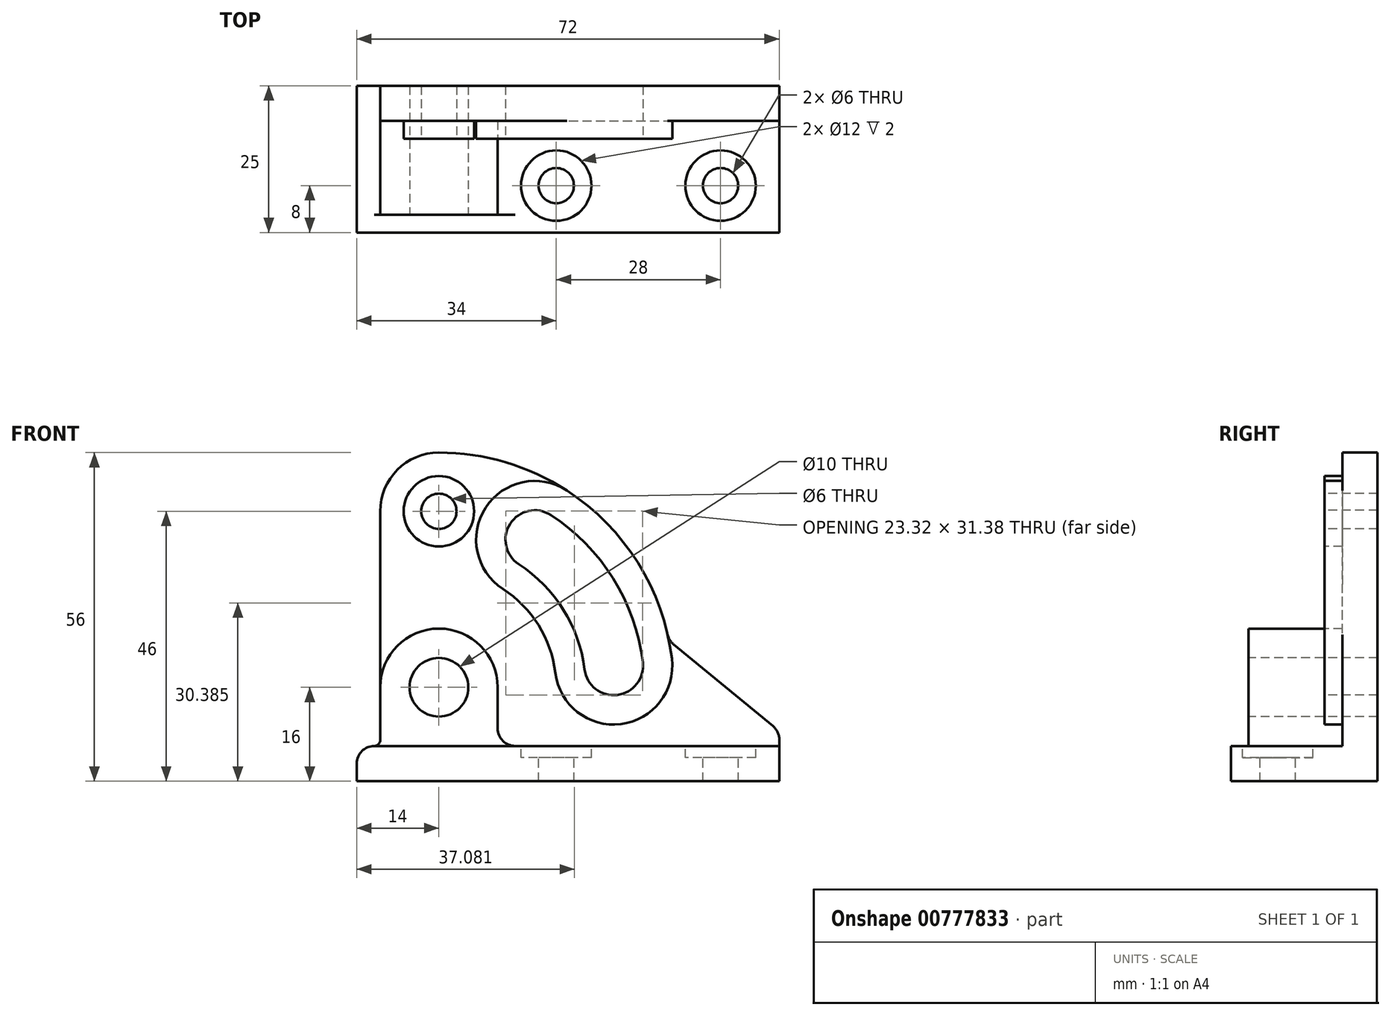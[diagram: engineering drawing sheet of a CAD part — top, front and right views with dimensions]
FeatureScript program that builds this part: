
annotation { "Feature Type Name" : "Feature", "Feature Type Description" : "" }
export const myFeature = defineFeature(function(context is Context, id is Id, definition is map)
    precondition{}
    {
        {
            var Q0;
            Q0=qCreatedBy(makeId("Front.planeOp"),FACE);
            var sketch = newSketch(context, id + "F0", { "sketchPlane" : qUnion([Q0])});
            skLineSegment(sketch, "E0", {"start": v(0, -16) * mm, "end": v(58, -16) * mm});
            skLineSegment(sketch, "E1", {"start": v(58, -16) * mm, "end": v(58, -8.92) * mm});
            skLineSegment(sketch, "E2", {"start": v(56.9, -6.6) * mm, "end": v(40, 7.34) * mm});
            skLineSegment(sketch, "E3", {"start": v(-14, -13) * mm, "end": v(-14, -16) * mm});
            skLineSegment(sketch, "E4", {"start": v(-14, -16) * mm, "end": v(0, -16) * mm});
            skLineSegment(sketch, "E5", {"start": v(-11, -10) * mm, "end": v(-11, -10) * mm});
            skLineSegment(sketch, "E6", {"start": v(-10, -9) * mm, "end": v(-10, 30) * mm});
            skLineSegment(sketch, "E7", {"start": v(0, 0) * mm, "end": v(0, 30) * mm, "construction": true});
            skArc(sketch, "E8", {"start": v(0, 40) * mm, "mid": v(-7.07, 37.07) * mm, "end": v(-10, 30) * mm});
            skArc(sketch, "E9", {"start": v(38.98, 8.98) * mm, "mid": v(24.9, 31.3) * mm, "end": v(0, 40) * mm});
            skLineSegment(sketch, "E10", {"start": v(0, 8) * mm, "end": v(65.06, 8) * mm, "construction": true});
            skPoint(sketch, "E11", {"position": v(0, 15) * mm});
            skPoint(sketch, "E12.visualSharp", {"position": v(58, -7.5) * mm});
            skArc(sketch, "E12.filletArc", {"start": v(58, -8.92) * mm, "mid": v(57.71, -7.64) * mm, "end": v(56.9, -6.6) * mm});
            skPoint(sketch, "E13.visualSharp", {"position": v(-14, -10) * mm});
            skArc(sketch, "E13.filletArc", {"start": v(-11, -10) * mm, "mid": v(-13.12, -10.88) * mm, "end": v(-14, -13) * mm});
            skPoint(sketch, "E14.visualSharp", {"position": v(39.2, 8) * mm});
            skArc(sketch, "E14.filletArc", {"start": v(38.98, 8.98) * mm, "mid": v(39.35, 8.08) * mm, "end": v(40, 7.34) * mm});
            skPoint(sketch, "E15.visualSharp", {"position": v(-10, -10) * mm});
            skArc(sketch, "E15.filletArc", {"start": v(-11, -10) * mm, "mid": v(-10.3, -9.7) * mm, "end": v(-10, -9) * mm});
            skSolve(sketch);
        }
        {
            var Q0;
            Q0 = qSketchRegion(id + "F0", true);
            extrude(context, id + "F1", {"entities" : qUnion([Q0]), "depth" : 25 * mm, "offsetDistance" : 25 * mm});
        }
        {
            var Q0;
            Q0=makeQuery(id+"F1.opExtrude","CAP_FACE",FACE,{"disambiguationData":[OSD([sQuery(id+"F0.wireOp",EDGE,"E0"),sQuery(id+"F0.wireOp",EDGE,"E1"),sQuery(id+"F0.wireOp",EDGE,"E2"),sQuery(id+"F0.wireOp",EDGE,"E3"),sQuery(id+"F0.wireOp",EDGE,"E4"),sQuery(id+"F0.wireOp",EDGE,"E6"),sQuery(id+"F0.wireOp",EDGE,"E8"),sQuery(id+"F0.wireOp",EDGE,"E9"),sQuery(id+"F0.wireOp",EDGE,"E12.filletArc"),sQuery(id+"F0.wireOp",EDGE,"E13.filletArc"),sQuery(id+"F0.wireOp",EDGE,"E14.filletArc"),sQuery(id+"F0.wireOp",EDGE,"E15.filletArc")])],"isStart":false});
            var sketch = newSketch(context, id + "F2", { "sketchPlane" : qUnion([Q0])});
            skArc(sketch, "E16", {"start": v(10, 0) * mm, "mid": v(0, 10) * mm, "end": v(-10, 0) * mm});
            skLineSegment(sketch, "E17", {"start": v(10, 0) * mm, "end": v(10, -7) * mm});
            skLineSegment(sketch, "E18", {"start": v(13, -10) * mm, "end": v(58, -10) * mm});
            skPoint(sketch, "E19.visualSharp", {"position": v(10, -10) * mm});
            skArc(sketch, "E19.filletArc", {"start": v(10, -7) * mm, "mid": v(10.88, -9.12) * mm, "end": v(13, -10) * mm});
            skCircle(sketch, "E20", {"center": v(0, 30) * mm, "radius": 6 * mm});
            skArc(sketch, "E21", {"start": v(0, 30) * mm, "mid": v(21.21, 21.21) * mm, "end": v(30, 0) * mm, "construction": true});
            skLineSegment(sketch, "E22", {"start": v(0, 0) * mm, "end": v(21.79, 33.55) * mm, "construction": true});
            skLineSegment(sketch, "E23", {"start": v(0, 0) * mm, "end": v(39.7, 4.87) * mm, "construction": true});
            skArc(sketch, "E24", {"start": v(21.79, 33.55) * mm, "mid": v(7.95, 30.6) * mm, "end": v(10.9, 16.77) * mm});
            skArc(sketch, "E25", {"start": v(19.85, 2.44) * mm, "mid": v(31, -6.27) * mm, "end": v(39.7, 4.87) * mm});
            skArc(sketch, "E26", {"start": v(10.9, 16.77) * mm, "mid": v(16.96, 10.6) * mm, "end": v(19.85, 2.44) * mm});
            skArc(sketch, "E27", {"start": v(38.98, 8.98) * mm, "mid": v(39.4, 6.94) * mm, "end": v(39.7, 4.87) * mm});
            skArc(sketch, "E28.0", {"start": v(38.98, 8.98) * mm, "mid": v(39.35, 8.08) * mm, "end": v(40, 7.34) * mm});
            skLineSegment(sketch, "E29.0", {"start": v(56.9, -6.6) * mm, "end": v(40, 7.34) * mm});
            skArc(sketch, "E30.0", {"start": v(58, -8.92) * mm, "mid": v(57.71, -7.64) * mm, "end": v(56.9, -6.6) * mm});
            skLineSegment(sketch, "E31.0", {"start": v(58, -10) * mm, "end": v(58, -8.92) * mm});
            skPoint(sketch, "E32.orphan", {"position": v(58, -16) * mm});
            skLineSegment(sketch, "E33.0", {"start": v(-10, 0) * mm, "end": v(-10, 30) * mm});
            skArc(sketch, "E34.0", {"start": v(0, 40) * mm, "mid": v(-7.07, 37.07) * mm, "end": v(-10, 30) * mm});
            skArc(sketch, "E35.0", {"start": v(21.79, 33.55) * mm, "mid": v(11.36, 38.35) * mm, "end": v(0, 40) * mm});
            skPoint(sketch, "E36.orphan", {"position": v(-10, -9) * mm});
            skSolve(sketch);
        }
        {
            var Q0;
            Q0 = qSketchRegion(id + "F2", true);
            extrude(context, id + "F3", {"entities" : qUnion([Q0]), "operationType" : NewBodyOperationType.REMOVE, "oppositeDirection" : true, "depth" : 19 * mm, "offsetDistance" : 25 * mm});
        }
        {
            var Q0;
            {var subQ0=sQuery(id+"F0.wireOp",EDGE,"E6");var subQ1=sQuery(id+"F0.wireOp",EDGE,"E3");var subQ2=sQuery(id+"F0.wireOp",EDGE,"E1");var subQ3=sQuery(id+"F0.wireOp",EDGE,"E4");var subQ4=sQuery(id+"F0.wireOp",EDGE,"E0");var subQ5=sQuery(id+"F0.wireOp",EDGE,"E13.filletArc");var subQ6=sQuery(id+"F0.wireOp",EDGE,"E15.filletArc");Q0=makeQuery(id+"F3.boolean.opBoolean","SPLIT",FACE,{"disambiguationData":[TD([makeQuery(id+"F1.opExtrude","SWEPT_FACE",FACE,{"disambiguationData":[OSD([subQ2])]})])],"derivedFrom":makeQuery(id+"F1.opExtrude","CAP_FACE",FACE,{"disambiguationData":[OSD([subQ4,subQ2,sQuery(id+"F0.wireOp",EDGE,"E2"),subQ1,subQ3,subQ0,sQuery(id+"F0.wireOp",EDGE,"E8"),sQuery(id+"F0.wireOp",EDGE,"E9"),sQuery(id+"F0.wireOp",EDGE,"E12.filletArc"),subQ5,sQuery(id+"F0.wireOp",EDGE,"E14.filletArc"),subQ6])],"isStart":false})});}
            var sketch = newSketch(context, id + "F4", { "sketchPlane" : qUnion([Q0])});
            skCircle(sketch, "E37.0", {"center": v(0, 30) * mm, "radius": 6 * mm});
            skArc(sketch, "E38.0", {"start": v(21.79, 33.55) * mm, "mid": v(7.95, 30.6) * mm, "end": v(10.9, 16.77) * mm});
            skArc(sketch, "E39.0", {"start": v(10.9, 16.77) * mm, "mid": v(16.96, 10.6) * mm, "end": v(19.85, 2.44) * mm});
            skArc(sketch, "E40.0", {"start": v(19.85, 2.44) * mm, "mid": v(31, -6.27) * mm, "end": v(39.7, 4.87) * mm});
            skArc(sketch, "E41.0", {"start": v(39.7, 4.87) * mm, "mid": v(33.92, 21.2) * mm, "end": v(21.79, 33.55) * mm});
            skSolve(sketch);
        }
        {
            var Q0;
            Q0 = qSketchRegion(id + "F4", true);
            extrude(context, id + "F5", {"entities" : qUnion([Q0]), "operationType" : NewBodyOperationType.REMOVE, "oppositeDirection" : true, "depth" : 16 * mm, "offsetDistance" : 25 * mm});
        }
        {
            var Q0;
            {var subQ0=sQuery(id+"F0.wireOp",EDGE,"E6");var subQ1=sQuery(id+"F0.wireOp",EDGE,"E3");var subQ2=sQuery(id+"F0.wireOp",EDGE,"E1");var subQ3=sQuery(id+"F0.wireOp",EDGE,"E4");var subQ4=sQuery(id+"F0.wireOp",EDGE,"E0");var subQ5=sQuery(id+"F0.wireOp",EDGE,"E13.filletArc");var subQ6=sQuery(id+"F0.wireOp",EDGE,"E15.filletArc");Q0=makeQuery(id+"F3.boolean.opBoolean","SPLIT",FACE,{"disambiguationData":[TD([makeQuery(id+"F1.opExtrude","SWEPT_FACE",FACE,{"disambiguationData":[OSD([subQ2])]})])],"derivedFrom":makeQuery(id+"F1.opExtrude","CAP_FACE",FACE,{"disambiguationData":[OSD([subQ4,subQ2,sQuery(id+"F0.wireOp",EDGE,"E2"),subQ1,subQ3,subQ0,sQuery(id+"F0.wireOp",EDGE,"E8"),sQuery(id+"F0.wireOp",EDGE,"E9"),sQuery(id+"F0.wireOp",EDGE,"E12.filletArc"),subQ5,sQuery(id+"F0.wireOp",EDGE,"E14.filletArc"),subQ6])],"isStart":false})});}
            var sketch = newSketch(context, id + "F6", { "sketchPlane" : qUnion([Q0])});
            skLineSegment(sketch, "E42", {"start": v(13, -10) * mm, "end": v(-11, -10) * mm});
            skArc(sketch, "E43.0", {"start": v(10, -7) * mm, "mid": v(10.88, -9.12) * mm, "end": v(13, -10) * mm});
            skLineSegment(sketch, "E44.0", {"start": v(10, 0) * mm, "end": v(10, -7) * mm});
            skArc(sketch, "E45.0", {"start": v(10, 0) * mm, "mid": v(0, 10) * mm, "end": v(-10, 0) * mm});
            skArc(sketch, "E46.0", {"start": v(-11, -10) * mm, "mid": v(-10.3, -9.7) * mm, "end": v(-10, -9) * mm});
            skLineSegment(sketch, "E47.0", {"start": v(-10, -9) * mm, "end": v(-10, 0) * mm});
            skSolve(sketch);
        }
        {
            var Q0;
            Q0 = qSketchRegion(id + "F6", true);
            extrude(context, id + "F7", {"entities" : qUnion([Q0]), "operationType" : NewBodyOperationType.REMOVE, "oppositeDirection" : true, "depth" : 3 * mm, "offsetDistance" : 25 * mm});
        }
        {
            var Q0;
            Q0=makeQuery(id+"F7.boolean.opBoolean","COPY",FACE,{"derivedFrom":makeQuery(id+"F7.opExtrude","CAP_FACE",FACE,{"disambiguationData":[OSD([sQuery(id+"F6.wireOp",EDGE,"E42"),sQuery(id+"F6.wireOp",EDGE,"E43.0"),sQuery(id+"F6.wireOp",EDGE,"E44.0"),sQuery(id+"F6.wireOp",EDGE,"E45.0"),sQuery(id+"F6.wireOp",EDGE,"E46.0"),sQuery(id+"F6.wireOp",EDGE,"E47.0")])],"isStart":false})});
            var sketch = newSketch(context, id + "F8", { "sketchPlane" : qUnion([Q0])});
            skPoint(sketch, "E48", {"position": v(0, 0) * mm});
            skSolve(sketch);
        }
        {
            var Q0;
            Q0=sQuery(id+"F8.wireOp",VERTEX,"E48");
            var Q1;
            Q1=makeQuery(id+"F1.opExtrude","SWEPT_BODY",BODY,{"disambiguationData":[OSD([sQuery(id+"F0.wireOp",EDGE,"E0"),sQuery(id+"F0.wireOp",EDGE,"E1"),sQuery(id+"F0.wireOp",EDGE,"E2"),sQuery(id+"F0.wireOp",EDGE,"E3"),sQuery(id+"F0.wireOp",EDGE,"E4"),sQuery(id+"F0.wireOp",EDGE,"E6"),sQuery(id+"F0.wireOp",EDGE,"E8"),sQuery(id+"F0.wireOp",EDGE,"E9"),sQuery(id+"F0.wireOp",EDGE,"E12.filletArc"),sQuery(id+"F0.wireOp",EDGE,"E13.filletArc"),sQuery(id+"F0.wireOp",EDGE,"E14.filletArc"),sQuery(id+"F0.wireOp",EDGE,"E15.filletArc")])]});
            hole(context, id + "F9", {"style" : HoleStyle.SIMPLE, "endStyle" : HoleEndStyle.THROUGH, "holeDiameter" : 10 * mm, "majorDiameter" : 5 * mm, "isTappedThrough" : true, "tappedDepth" : 12 * mm, "tapClearance" : 3, "locations" : qUnion([Q0]), "scope" : qUnion([Q1])});
        }
        {
            var Q0;
            Q0=makeQuery(id+"F5.boolean.opBoolean","COPY",FACE,{"derivedFrom":makeQuery(id+"F5.opExtrude","CAP_FACE",FACE,{"disambiguationData":[OSD([sQuery(id+"F4.wireOp",EDGE,"E37.0")])],"isStart":false})});
            var sketch = newSketch(context, id + "F10", { "sketchPlane" : qUnion([Q0])});
            skPoint(sketch, "E49", {"position": v(0, 30) * mm});
            skSolve(sketch);
        }
        {
            var Q0;
            Q0=sQuery(id+"F10.wireOp",VERTEX,"E49");
            var Q1;
            Q1=makeQuery(id+"F1.opExtrude","SWEPT_BODY",BODY,{"disambiguationData":[OSD([sQuery(id+"F0.wireOp",EDGE,"E0"),sQuery(id+"F0.wireOp",EDGE,"E1"),sQuery(id+"F0.wireOp",EDGE,"E2"),sQuery(id+"F0.wireOp",EDGE,"E3"),sQuery(id+"F0.wireOp",EDGE,"E4"),sQuery(id+"F0.wireOp",EDGE,"E6"),sQuery(id+"F0.wireOp",EDGE,"E8"),sQuery(id+"F0.wireOp",EDGE,"E9"),sQuery(id+"F0.wireOp",EDGE,"E12.filletArc"),sQuery(id+"F0.wireOp",EDGE,"E13.filletArc"),sQuery(id+"F0.wireOp",EDGE,"E14.filletArc"),sQuery(id+"F0.wireOp",EDGE,"E15.filletArc")])]});
            hole(context, id + "F11", {"style" : HoleStyle.SIMPLE, "endStyle" : HoleEndStyle.THROUGH, "holeDiameter" : 6 * mm, "majorDiameter" : 5 * mm, "isTappedThrough" : true, "tappedDepth" : 12 * mm, "tapClearance" : 3, "locations" : qUnion([Q0]), "scope" : qUnion([Q1])});
        }
        {
            var Q0;
            Q0=makeQuery(id+"F5.boolean.opBoolean","COPY",FACE,{"derivedFrom":makeQuery(id+"F5.opExtrude","CAP_FACE",FACE,{"disambiguationData":[OSD([sQuery(id+"F4.wireOp",EDGE,"E38.0"),sQuery(id+"F4.wireOp",EDGE,"E39.0"),sQuery(id+"F4.wireOp",EDGE,"E40.0"),sQuery(id+"F4.wireOp",EDGE,"E41.0")])],"isStart":false})});
            var sketch = newSketch(context, id + "F12", { "sketchPlane" : qUnion([Q0])});
            skArc(sketch, "E50", {"start": v(19.06, 29.35) * mm, "mid": v(12.15, 27.88) * mm, "end": v(13.62, 20.97) * mm});
            skArc(sketch, "E51", {"start": v(24.81, 3.05) * mm, "mid": v(30.39, -1.3) * mm, "end": v(34.74, 4.27) * mm});
            skArc(sketch, "E52", {"start": v(13.62, 20.97) * mm, "mid": v(21.2, 13.25) * mm, "end": v(24.81, 3.05) * mm});
            skArc(sketch, "E53", {"start": v(19.06, 29.35) * mm, "mid": v(29.68, 18.55) * mm, "end": v(34.74, 4.27) * mm});
            skSolve(sketch);
        }
        {
            var Q0;
            Q0 = qSketchRegion(id + "F12", true);
            extrude(context, id + "F13", {"entities" : qUnion([Q0]), "operationType" : NewBodyOperationType.REMOVE, "oppositeDirection" : true, "depth" : 9 * mm, "offsetDistance" : 25 * mm});
        }
        {
            var Q0;
            Q0=makeQuery(id+"F7.boolean.opBoolean","MERGE",FACE,{"derivedFrom":[makeQuery(id+"F3.boolean.opBoolean","COPY",FACE,{"derivedFrom":makeQuery(id+"F3.opExtrude","SWEPT_FACE",FACE,{"disambiguationData":[OSD([sQuery(id+"F2.wireOp",EDGE,"E18")])]})}),makeQuery(id+"F7.opExtrude","SWEPT_FACE",FACE,{"disambiguationData":[OSD([sQuery(id+"F6.wireOp",EDGE,"E42")])]})]});
            var sketch = newSketch(context, id + "F14", { "sketchPlane" : qUnion([Q0])});
            skPoint(sketch, "E54", {"position": v(20, -17) * mm});
            skPoint(sketch, "E55", {"position": v(48, -17) * mm});
            skSolve(sketch);
        }
        {
            var Q0;
            Q0=sQuery(id+"F14.wireOp",VERTEX,"E54");
            var Q1;
            Q1=sQuery(id+"F14.wireOp",VERTEX,"E55");
            var Q2;
            Q2=makeQuery(id+"F1.opExtrude","SWEPT_BODY",BODY,{"disambiguationData":[OSD([sQuery(id+"F0.wireOp",EDGE,"E0"),sQuery(id+"F0.wireOp",EDGE,"E1"),sQuery(id+"F0.wireOp",EDGE,"E2"),sQuery(id+"F0.wireOp",EDGE,"E3"),sQuery(id+"F0.wireOp",EDGE,"E4"),sQuery(id+"F0.wireOp",EDGE,"E6"),sQuery(id+"F0.wireOp",EDGE,"E8"),sQuery(id+"F0.wireOp",EDGE,"E9"),sQuery(id+"F0.wireOp",EDGE,"E12.filletArc"),sQuery(id+"F0.wireOp",EDGE,"E13.filletArc"),sQuery(id+"F0.wireOp",EDGE,"E14.filletArc"),sQuery(id+"F0.wireOp",EDGE,"E15.filletArc")])]});
            hole(context, id + "F15", {"style" : HoleStyle.C_BORE, "endStyle" : HoleEndStyle.THROUGH, "holeDiameter" : 6 * mm, "cBoreDiameter" : 12 * mm, "cBoreDepth" : 2 * mm, "majorDiameter" : 5 * mm, "isTappedThrough" : true, "tappedDepth" : 12 * mm, "tapClearance" : 3, "locations" : qUnion([Q0, Q1]), "scope" : qUnion([Q2])});
        }
    });
